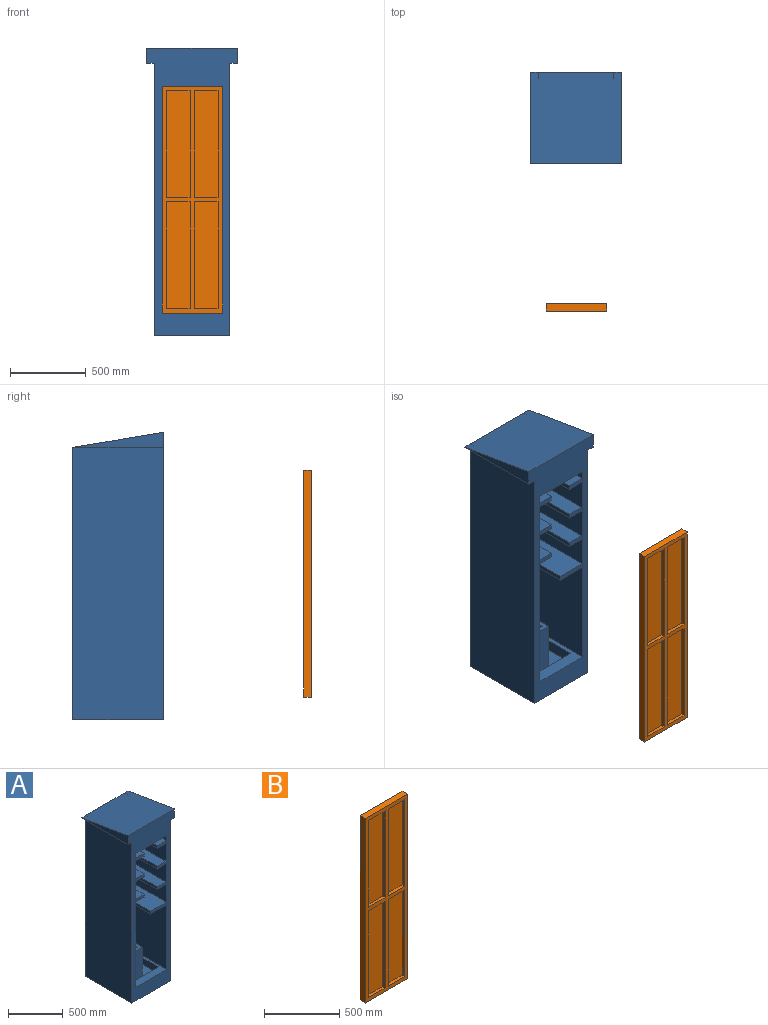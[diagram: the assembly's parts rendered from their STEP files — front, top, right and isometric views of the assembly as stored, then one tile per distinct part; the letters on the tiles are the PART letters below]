
ASSEMBLY  parts=2 mates=1
PART A: 63 faces, bbox 600x600x1900 mm
  f0: plane 208.57x76mm, normal (0,-1,0), area 15851.6mm2, adj f4,f26,f27,f59
  f1: plane 208.57x76mm, normal (0,1,0), area 15851.6mm2, adj f11,f26,f27,f59
  f2: plane 384.95x113.48mm, normal (0,0,1), area 43683.5mm2, adj f24,f25,f60,f61
  f3: plane 1410x400mm, normal (0,-1,0), area 524476.7mm2, adj f4,f9,f11,f22,f23,f29,f31,f32
  f4: plane 208.57x16.21mm, normal (0,0,-1), area 3380.6mm2, adj f0,f3,f26,f59
  f5: plane 483x400mm, normal (0,0,-1), area 37132.8mm2, adj f9,f10,f12,f22,f52,f53
  f6: plane 113.09x30mm, normal (0,-1,0), area 3392.6mm2, adj f9,f28,f29,f50
  f7: plane 113.09x30mm, normal (0,-1,0), area 3392.6mm2, adj f9,f31,f32,f47
  f8: plane 113.09x30mm, normal (0,-1,0), area 3392.6mm2, adj f9,f35,f36,f44
  f9: plane 1577x493.99mm, normal (1,0,0), area 712753.5mm2, adj f3,f5,f6,f7,f8,f10,f11,f12
  f10: plane 400x60mm, normal (0,-1,0), area 24000mm2, adj f5,f9,f22,f28,f56
  f11: plane 483x400mm, normal (0,0,1), area 52770.8mm2, adj f1,f3,f9,f12,f22,f25,f26,f57
  f12: plane 1900x600mm, normal (0,-1,0), area 360000mm2, adj f5,f9,f11,f13,f15,f16,f17,f18
  f13: plane 600x100mm, normal (-1,0,0), area 30000mm2, adj f12,f18,f21
  f14: plane 1800x500mm, normal (0,1,0), area 900000mm2, adj f15,f16,f17,f21
  f15: plane 1800x600mm, normal (-1,0,0), area 1080000mm2, adj f12,f14,f17,f18
  f16: plane 1800x600mm, normal (1,0,0), area 1080000mm2, adj f12,f14,f17,f20
  f17: plane 600x500mm, normal (0,0,-1), area 300000mm2, adj f12,f14,f15,f16
  f18: plane 600x50mm, normal (0,0,-1), area 30000mm2, adj f12,f13,f15,f21
  f19: plane 600x100mm, normal (1,0,0), area 30000mm2, adj f12,f20,f21
  f20: plane 600x50mm, normal (0,0,-1), area 30000mm2, adj f12,f16,f19,f21
  f21: plane 600x600mm, normal (0,0.16,0.99), area 364965.8mm2, adj f12,f13,f14,f18,f19,f20
  f22: plane 1500x483mm, normal (-1,0,0), area 695880mm2, adj f3,f5,f10,f11,f12,f28,f29,f30
  f23: plane 113.48x16.21mm, normal (0,0,-1), area 1839.3mm2, adj f3,f24,f25,f60
  f24: plane 113.48x76mm, normal (0,-1,0), area 8624.4mm2, adj f2,f23,f25,f60
  f25: plane 384.95x76mm, normal (1,0,0), area 29256.1mm2, adj f2,f11,f23,f24,f61
  f26: plane 415.42x76mm, normal (-1,0,0), area 31571.7mm2, adj f0,f1,f4,f11,f27
  f27: plane 415.42x208.57mm, normal (0,0,1), area 86644.8mm2, adj f0,f1,f26,f59
  f28: plane 477x400mm, normal (0,0,1), area 131725.1mm2, adj f6,f9,f10,f22,f30,f49,f50,f51
  f29: plane 477x400mm, normal (0,0,-1), area 131725.1mm2, adj f3,f6,f9,f22,f30,f49,f50,f51
  f30: plane 116.97x30mm, normal (0,-1,0), area 3509mm2, adj f22,f28,f29,f51
  f31: plane 477x396.12mm, normal (0,0,1), area 129873.9mm2, adj f3,f7,f9,f33,f34,f46,f47,f48
  f32: plane 477x396.12mm, normal (0,0,-1), area 129873.9mm2, adj f3,f7,f9,f33,f34,f46,f47,f48
  f33: plane 477x30mm, normal (1,0,0), area 14310mm2, adj f3,f31,f32,f34
  f34: plane 113.09x30mm, normal (0,-1,0), area 3392.6mm2, adj f31,f32,f33,f46
  f35: plane 477x396.12mm, normal (0,0,1), area 129873.9mm2, adj f3,f8,f9,f37,f38,f43,f44,f45
  f36: plane 477x396.12mm, normal (0,0,-1), area 129873.9mm2, adj f3,f8,f9,f37,f38,f43,f44,f45
  f37: plane 477x30mm, normal (1,0,0), area 14310mm2, adj f3,f35,f36,f38
  f38: plane 113.09x30mm, normal (0,-1,0), area 3392.6mm2, adj f35,f36,f37,f43
  f39: plane 477x204.26mm, normal (0,0,1), area 97432.2mm2, adj f3,f22,f40,f42
  f40: plane 477x30mm, normal (-1,0,0), area 14310mm2, adj f3,f39,f41,f42
  f41: plane 477x204.26mm, normal (0,0,-1), area 97432.2mm2, adj f3,f22,f40,f42
  f42: plane 204.26x30mm, normal (0,-1,0), area 6127.8mm2, adj f22,f39,f40,f41
  f43: plane 347.61x30mm, normal (-1,0,0), area 10428.3mm2, adj f35,f36,f38,f45
  f44: plane 347.61x30mm, normal (1,0,0), area 10428.3mm2, adj f8,f35,f36,f45
  f45: plane 169.95x30mm, normal (0,-1,0), area 5098.4mm2, adj f35,f36,f43,f44
  f46: plane 347.61x30mm, normal (-1,0,0), area 10428.3mm2, adj f31,f32,f34,f48
  f47: plane 347.61x30mm, normal (1,0,0), area 10428.3mm2, adj f7,f31,f32,f48
  f48: plane 169.95x30mm, normal (0,-1,0), area 5098.4mm2, adj f31,f32,f46,f47
  f49: plane 169.95x30mm, normal (0,-1,0), area 5098.4mm2, adj f28,f29,f50,f51
  f50: plane 347.61x30mm, normal (1,0,0), area 10428.3mm2, adj f6,f28,f29,f49
  f51: plane 347.61x30mm, normal (-1,0,0), area 10428.3mm2, adj f28,f29,f30,f49
  f52: plane 404.98x77mm, normal (-1,0,0), area 31183.5mm2, adj f5,f53,f54,f55,f56
  f53: plane 396.12x77mm, normal (0,1,0), area 30501.2mm2, adj f5,f9,f52,f55
  f54: plane 396.12x77mm, normal (0,-1,0), area 30501.2mm2, adj f9,f52,f55,f56
  f55: plane 404.98x396.12mm, normal (0,0,-1), area 160420.8mm2, adj f9,f52,f53,f54
  f56: plane 396.12x10.99mm, normal (0,0,1), area 4353.6mm2, adj f9,f10,f52,f54
  f57: plane 324x143.2mm, normal (0,-1,0), area 46395.5mm2, adj f11,f58,f59,f62
  f58: plane 324x30.47mm, normal (-1,0,0), area 9871.7mm2, adj f11,f57,f61,f62
  f59: plane 415.42x400mm, normal (1,0,0), area 160915.1mm2, adj f0,f1,f3,f4,f27,f57,f62
  f60: plane 400x384.95mm, normal (-1,0,0), area 148727.9mm2, adj f2,f3,f23,f24,f61,f62
  f61: plane 400x113.48mm, normal (0,1,0), area 45391.6mm2, adj f2,f25,f58,f60,f62
  f62: plane 399.21x143.2mm, normal (0,0,1), area 15320.8mm2, adj f3,f57,f58,f59,f60,f61
PART B: 26 faces, bbox 400x50x1500 mm
  f0: plane 155.02x25mm, normal (0,0,-1), area 3875.4mm2, adj f2,f19,f21,f24
  f1: plane 155.05x25mm, normal (0,0,1), area 3876.2mm2, adj f5,f16,f21,f23
  f2: plane 705.31x155.02mm, normal (0,-1,0), area 109333.9mm2, adj f0,f6,f19,f24
  f3: plane 705.31x155.02mm, normal (0,-1,0), area 109333.9mm2, adj f13,f14,f15,f25
  f4: plane 705.31x154.98mm, normal (0,-1,0), area 109312.3mm2, adj f7,f18,f20,f22
  f5: plane 705.31x155.05mm, normal (0,-1,0), area 109355.6mm2, adj f1,f16,f17,f23
  f6: plane 155.02x25mm, normal (0,0,1), area 3875.4mm2, adj f2,f19,f21,f24
  f7: plane 154.98x25mm, normal (0,0,-1), area 3874.6mm2, adj f4,f18,f21,f22
  f8: plane 1500x50mm, normal (-1,0,0), area 75000mm2, adj f9,f11,f12,f21
  f9: plane 400x50mm, normal (0,0,-1), area 20000mm2, adj f8,f10,f12,f21
  f10: plane 1500x50mm, normal (1,0,0), area 75000mm2, adj f9,f11,f12,f21
  f11: plane 400x50mm, normal (0,0,1), area 20000mm2, adj f8,f10,f12,f21
  f12: plane 1500x400mm, normal (0,1,0), area 600000mm2, adj f8,f9,f10,f11
  f13: plane 155.02x25mm, normal (0,0,1), area 3875.4mm2, adj f3,f14,f21,f25
  f14: plane 705.31x25mm, normal (1,0,0), area 17632.8mm2, adj f3,f13,f15,f21
  f15: plane 155.02x25mm, normal (0,0,-1), area 3875.4mm2, adj f3,f14,f21,f25
  f16: plane 705.31x25mm, normal (1,0,0), area 17632.8mm2, adj f1,f5,f17,f21
  f17: plane 155.05x25mm, normal (0,0,-1), area 3876.2mm2, adj f5,f16,f21,f23
  f18: plane 705.31x25mm, normal (-1,0,0), area 17632.8mm2, adj f4,f7,f20,f21
  f19: plane 705.31x25mm, normal (-1,0,0), area 17632.8mm2, adj f0,f2,f6,f21
  f20: plane 154.98x25mm, normal (0,0,1), area 3874.6mm2, adj f4,f18,f21,f22
  f21: plane 1500x400mm, normal (0,-1,0), area 162664.2mm2, adj f0,f1,f6,f7,f8,f9,f10,f11
  f22: plane 705.31x25mm, normal (1,0,0), area 17632.8mm2, adj f4,f7,f20,f21
  f23: plane 705.31x25mm, normal (-1,0,0), area 17632.8mm2, adj f1,f5,f17,f21
  f24: plane 705.31x25mm, normal (1,0,0), area 17632.8mm2, adj f0,f2,f6,f21
  f25: plane 705.31x25mm, normal (-1,0,0), area 17632.8mm2, adj f3,f13,f15,f21
PLACE A t=(-525.76,0,20.41)mm fixed
PLACE B t=(-523.82,-1227.15,920.41)mm
MATE slider B.f21 <-> A.f12  axis (0,-1,0) through (-523.82,-1277.15,1670.41)mm
